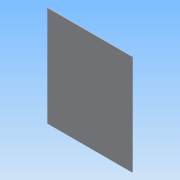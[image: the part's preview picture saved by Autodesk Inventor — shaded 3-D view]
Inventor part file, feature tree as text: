
AUTODESK INVENTOR PART (.ipt)
format: ipt  version: 2015 (Build 190159000, 159)  size: 83,456 bytes
history: native  units: in
note: dims shown in document units (in); Inventor stores cm internally (conversion verified against a paired STEP export)
features: reference x2, extrude x1, sketch x1
ambient origin geometry x8: Origin, YZ Plane, XZ Plane, XY Plane, X Axis, Y Axis, Z Axis, Center Point
bodies: Solid1 (feature_tree)
feature tree (4):
  extrude  "Extrusion1"  [1 undecoded]
  sketch  "Sketch1"  dims[d0=0.0625in d1=0.0in]
  reference  "Reference1"
  reference  "Reference2"
note: 1 required parameter value undecoded (feature->parameter linkage not recoverable at this tier; creation-order binding heuristic only, values carry confidence <= 0.55)
